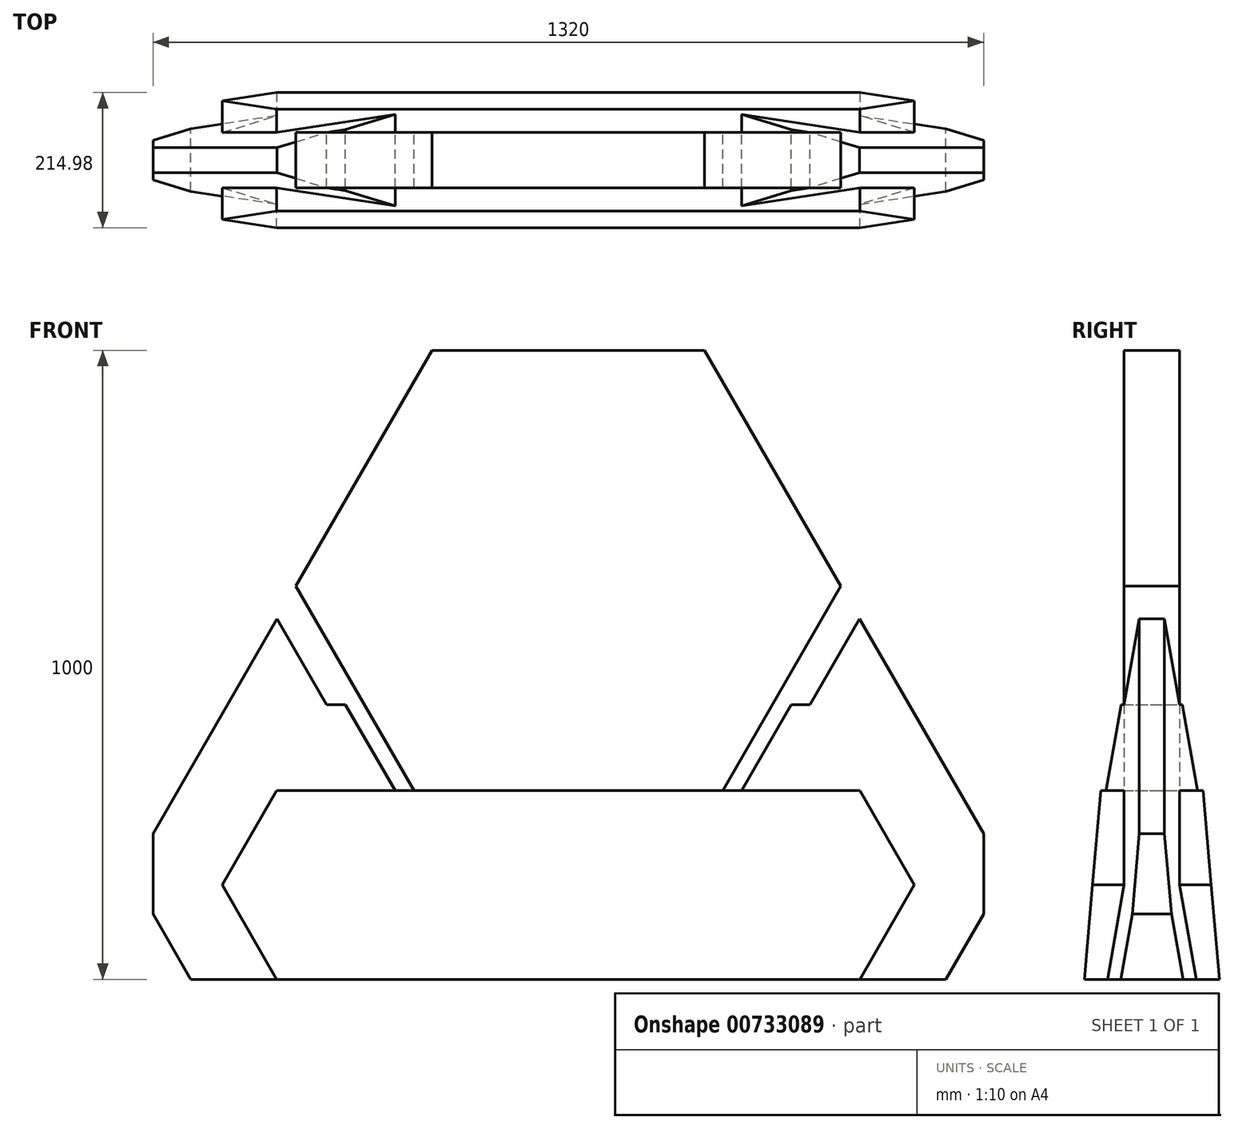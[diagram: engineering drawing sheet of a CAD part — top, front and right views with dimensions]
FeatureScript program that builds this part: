
annotation { "Feature Type Name" : "Feature", "Feature Type Description" : "" }
export const myFeature = defineFeature(function(context is Context, id is Id, definition is map)
    precondition{}
    {
        {
            var Q0;
            Q0=qCreatedBy(makeId("Front.planeOp"),FACE);
            var sketch = newSketch(context, id + "F0", { "sketchPlane" : qUnion([Q0])});
            skLineSegment(sketch, "E0", {"start": v(0, 0) * mm, "end": v(0, 1000) * mm});
            skCircle(sketch, "E1.cCircle", {"center": v(0, 625) * mm, "radius": 375 * mm, "construction": true});
            skLineSegment(sketch, "E1.0", {"start": v(0, 1000) * mm, "end": v(216.5, 1000) * mm});
            skLineSegment(sketch, "E1.1", {"start": v(216.5, 1000) * mm, "end": v(433.01, 625) * mm});
            skLineSegment(sketch, "E1.2", {"start": v(433.01, 625) * mm, "end": v(216.5, 250) * mm});
            skLineSegment(sketch, "E1.3", {"start": v(216.5, 250) * mm, "end": v(0, 250) * mm});
            skPoint(sketch, "E1.0.midPoint", {"position": v(0, 1000) * mm});
            skLineSegment(sketch, "E2", {"start": v(0, 0) * mm, "end": v(600, 0) * mm});
            skLineSegment(sketch, "E3", {"start": v(660, 103.92) * mm, "end": v(660, 231.85) * mm});
            skLineSegment(sketch, "E4", {"start": v(660, 231.85) * mm, "end": v(463.01, 573.04) * mm});
            skLineSegment(sketch, "E5", {"start": v(463.01, 573.04) * mm, "end": v(384.2, 436.52) * mm});
            skLineSegment(sketch, "E6", {"start": v(384.2, 436.52) * mm, "end": v(354.2, 436.52) * mm});
            skLineSegment(sketch, "E7", {"start": v(354.2, 436.52) * mm, "end": v(275.37, 300) * mm});
            skLineSegment(sketch, "E8", {"start": v(0, 300) * mm, "end": v(463.4, 300) * mm});
            skLineSegment(sketch, "E9", {"start": v(463.4, 300) * mm, "end": v(550, 150) * mm});
            skLineSegment(sketch, "E10", {"start": v(550, 150) * mm, "end": v(463.4, 0) * mm});
            skLineSegment(sketch, "E11", {"start": v(600, 0) * mm, "end": v(660, 103.92) * mm});
            skPoint(sketch, "E12.orphan", {"position": v(660, 0) * mm});
            skLineSegment(sketch, "E13", {"start": v(0, 300) * mm, "end": v(0, 0) * mm});
            skPoint(sketch, "E14.orphan", {"position": v(-216.5, 1000) * mm});
            skLineSegment(sketch, "E15", {"start": v(273.53, 348.77) * mm, "end": v(303.53, 348.77) * mm, "construction": true});
            skSolve(sketch);
        }
        {
            var Q0;
            {var subQ6=sQuery(id+"F0.wireOp",EDGE,"E1.0");Q0=makeQuery(id+"F0.imprint","IMPRINT",FACE,{"disambiguationData":[TD([[makeQuery(id+"F0.imprint","IMPRINT",EDGE,{"derivedFrom":subQ6}),-1.0]])]});}
            extrude(context, id + "F1", {"entities" : qUnion([Q0]), "depth" : 44 * mm, "offsetDistance" : 25 * mm});
        }
        {
            var Q0;
            Q0=sQuery(id+"F0.wireOp",EDGE,"E1.0");
            cPlane(context, id + "F2", {"entities" : qUnion([Q0]), "cplaneType" : CPlaneType.LINE_ANGLE, "offset" : 25 * mm, "angle" : 5 * degree, "oppositeDirection" : true, "width" : 150 * mm, "height" : 150 * mm});
        }
        {
            var Q0;
            {var subQ3=sQuery(id+"F0.wireOp",EDGE,"E1.3");Q0=makeQuery(id+"F0.imprint","IMPRINT",FACE,{"disambiguationData":[TD([[makeQuery(id+"F0.imprint","IMPRINT",EDGE,{"derivedFrom":subQ3}),-1.0]])]});}
            var Q1;
            {var subQ4=sQuery(id+"F0.wireOp",EDGE,"E1.3");Q1=makeQuery(id+"F0.imprint","IMPRINT",FACE,{"disambiguationData":[TD([[makeQuery(id+"F0.imprint","IMPRINT",EDGE,{"derivedFrom":subQ4}),1.0]])]});}
            var Q2;
            Q2=qCreatedBy(id+"F2.planeOp",FACE);
            extrude(context, id + "F3", {"entities" : qUnion([Q0, Q1]), "operationType" : NewBodyOperationType.ADD, "endBound" : BoundingType.UP_TO_SURFACE, "depth" : 25 * mm, "endBoundEntityFace" : qUnion([Q2]), "hasOffset" : true, "offsetDistance" : 20 * mm, "offsetOppositeDirection" : true});
        }
        {
            var Q0;
            Q0=sQuery(id+"F0.wireOp",EDGE,"E4");
            cPlane(context, id + "F4", {"entities" : qUnion([Q0]), "cplaneType" : CPlaneType.LINE_ANGLE, "offset" : 25 * mm, "angle" : 80 * degree, "oppositeDirection" : true, "width" : 150 * mm, "height" : 150 * mm});
        }
        {
            var Q0;
            Q0=makeQuery(id+"F0.imprint","IMPRINT",FACE,{"disambiguationData":[TD([[makeQuery(id+"F0.imprint","IMPRINT",EDGE,{"derivedFrom":sQuery(id+"F0.wireOp",EDGE,"E3")}),1.0]])]});
            var Q1;
            Q1=qCreatedBy(id+"F4.planeOp",FACE);
            extrude(context, id + "F5", {"entities" : qUnion([Q0]), "operationType" : NewBodyOperationType.ADD, "endBound" : BoundingType.UP_TO_SURFACE, "depth" : 25 * mm, "endBoundEntityFace" : qUnion([Q1]), "hasOffset" : true, "offsetDistance" : 20 * mm, "offsetOppositeDirection" : true});
        }
        {
            var Q0;
            Q0=makeQuery(id+"F1.opExtrude","SWEPT_BODY",BODY,{"disambiguationData":[OSD([sQuery(id+"F0.wireOp",EDGE,"E0"),sQuery(id+"F0.wireOp",EDGE,"E1.0"),sQuery(id+"F0.wireOp",EDGE,"E1.1"),sQuery(id+"F0.wireOp",EDGE,"E1.2"),sQuery(id+"F0.wireOp",EDGE,"E8")])]});
            var Q1;
            Q1=qCreatedBy(makeId("Right.planeOp"),FACE);
            mirror(context, id + "F6", {"operationType" : NewBodyOperationType.ADD, "entities" : qUnion([Q0]), "mirrorPlane" : qUnion([Q1])});
        }
        {
            var Q0;
            Q0=makeQuery(id+"F1.opExtrude","SWEPT_BODY",BODY,{"disambiguationData":[OSD([sQuery(id+"F0.wireOp",EDGE,"E0"),sQuery(id+"F0.wireOp",EDGE,"E1.0"),sQuery(id+"F0.wireOp",EDGE,"E1.1"),sQuery(id+"F0.wireOp",EDGE,"E1.2"),sQuery(id+"F0.wireOp",EDGE,"E8")])]});
            var Q1;
            Q1=qCreatedBy(makeId("Front.planeOp"),FACE);
            mirror(context, id + "F7", {"operationType" : NewBodyOperationType.ADD, "entities" : qUnion([Q0]), "mirrorPlane" : qUnion([Q1])});
        }
    });
